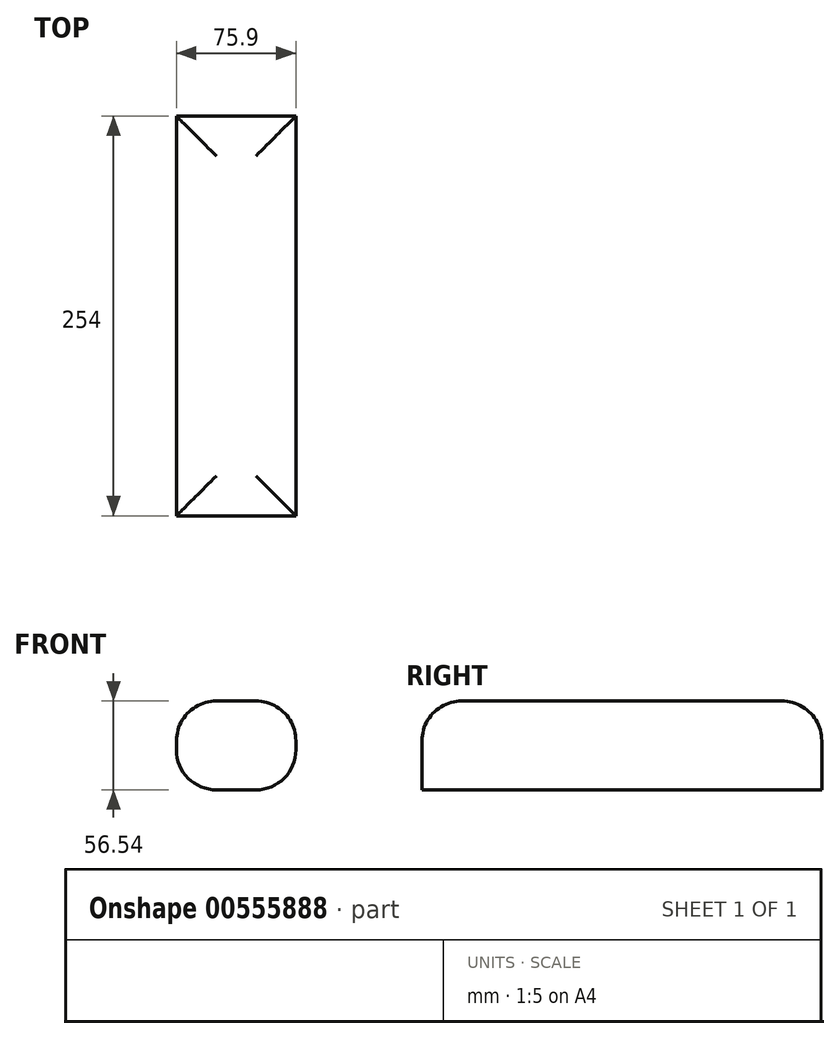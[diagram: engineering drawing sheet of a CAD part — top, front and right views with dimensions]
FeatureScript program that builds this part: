
annotation { "Feature Type Name" : "Feature", "Feature Type Description" : "" }
export const myFeature = defineFeature(function(context is Context, id is Id, definition is map)
    precondition{}
    {
        {
            var Q0;
            Q0=qCreatedBy(makeId("Front.planeOp"),FACE);
            var sketch = newSketch(context, id + "F0", { "sketchPlane" : qUnion([Q0])});
            skLineSegment(sketch, "E0", {"start": v(0, 0) * mm, "end": v(-75.9, 0) * mm});
            skLineSegment(sketch, "E1", {"start": v(-75.9, 0) * mm, "end": v(-75.9, 56.54) * mm});
            skLineSegment(sketch, "E2", {"start": v(-75.9, 56.54) * mm, "end": v(0, 56.54) * mm});
            skLineSegment(sketch, "E3", {"start": v(0, 56.54) * mm, "end": v(0, 0) * mm});
            skSolve(sketch);
        }
        {
            var Q0;
            Q0=makeQuery(id+"F0.imprint","IMPRINT",FACE,{"disambiguationData":[TD([[makeQuery(id+"F0.imprint","IMPRINT",EDGE,{"derivedFrom":sQuery(id+"F0.wireOp",EDGE,"E0")}),-1.0]])]});
            extrude(context, id + "F1", {"entities" : qUnion([Q0]), "depth" : 254 * mm, "offsetDistance" : 25.4 * mm});
        }
        {
            var Q0;
            Q0=makeQuery(id+"F1.opExtrude","SWEPT_EDGE",EDGE,{"disambiguationData":[OSD([sQuery(id+"F0.wireOp",EDGE,"E2"),sQuery(id+"F0.wireOp",EDGE,"E3")])]});
            var Q1;
            Q1=makeQuery(id+"F1.opExtrude","SWEPT_EDGE",EDGE,{"disambiguationData":[OSD([sQuery(id+"F0.wireOp",EDGE,"E0"),sQuery(id+"F0.wireOp",EDGE,"E3")])]});
            var Q2;
            Q2=makeQuery(id+"F1.opExtrude","SWEPT_FACE",FACE,{"disambiguationData":[OSD([sQuery(id+"F0.wireOp",EDGE,"E2")])]});
            var Q3;
            Q3=makeQuery(id+"F1.opExtrude","SWEPT_EDGE",EDGE,{"disambiguationData":[OSD([sQuery(id+"F0.wireOp",EDGE,"E0"),sQuery(id+"F0.wireOp",EDGE,"E1")])]});
            fillet(context, id + "F2", {"entities" : qUnion([Q0, Q1, Q2, Q3]), "radius" : 25.4 * mm, "tangentPropagation" : true, "allowEdgeOverflow" : false});
        }
    });
